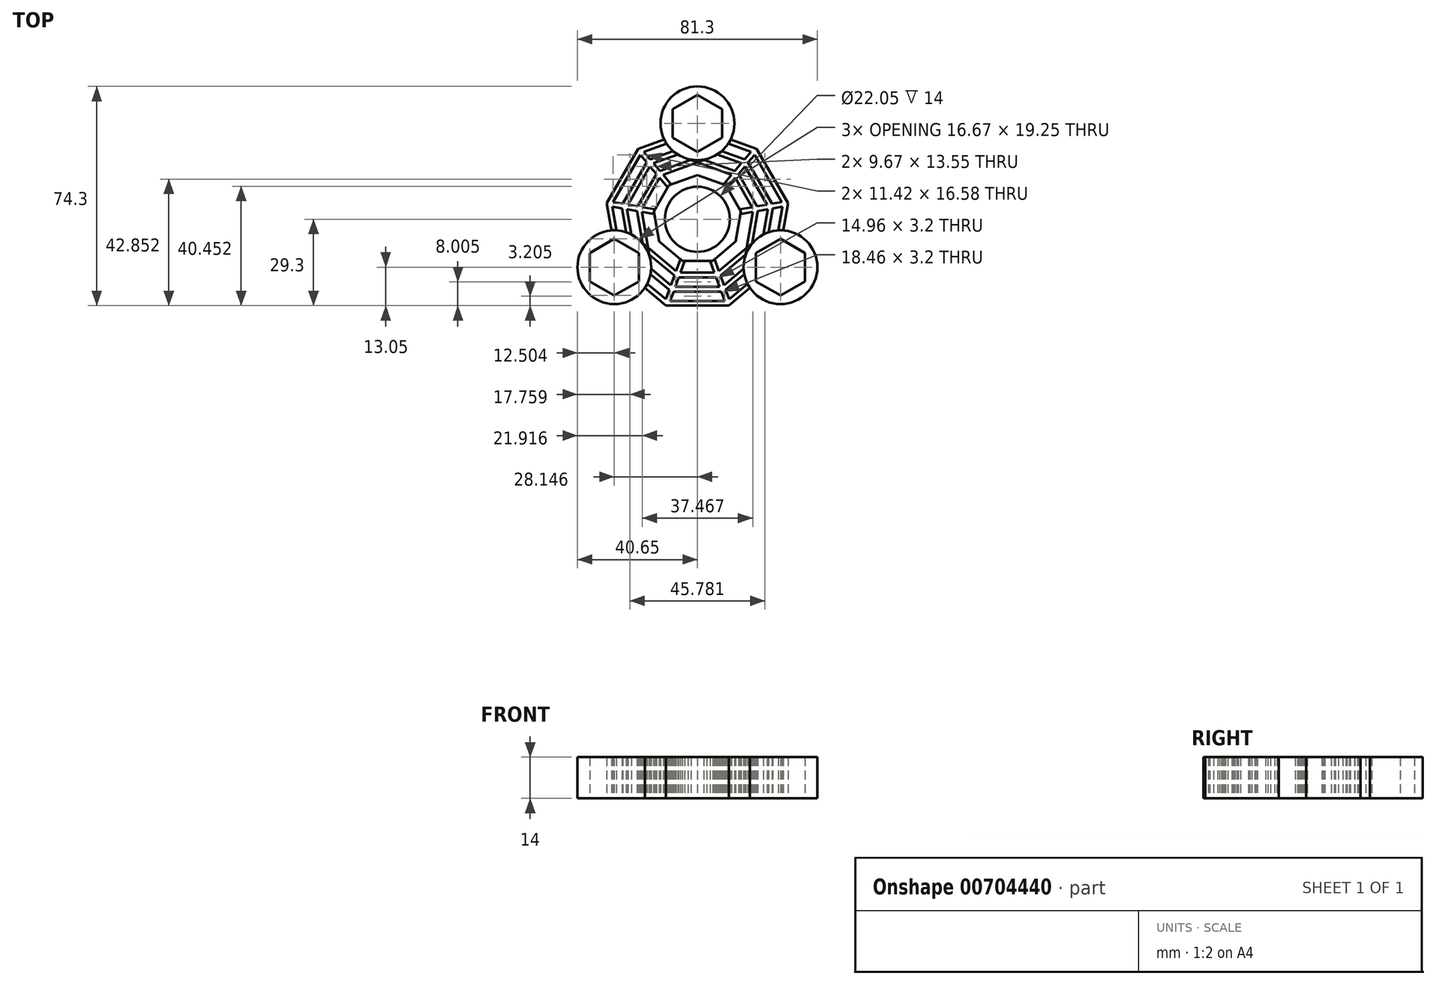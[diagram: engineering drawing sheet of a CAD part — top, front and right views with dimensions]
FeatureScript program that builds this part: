
annotation { "Feature Type Name" : "Feature", "Feature Type Description" : "" }
export const myFeature = defineFeature(function(context is Context, id is Id, definition is map)
    precondition{}
    {
        {
            var Q0;
            Q0=qCreatedBy(makeId("Top.planeOp"),FACE);
            var sketch = newSketch(context, id + "F0", { "sketchPlane" : qUnion([Q0])});
            skCircle(sketch, "E0", {"center": v(0, 0) * mm, "radius": 11.03 * mm});
            skCircle(sketch, "E1.cCircle", {"center": v(0, 32.5) * mm, "radius": 9.62 * mm, "construction": true});
            skLineSegment(sketch, "E1.0", {"start": v(8.34, 27.69) * mm, "end": v(0, 22.87) * mm});
            skLineSegment(sketch, "E1.1", {"start": v(0, 22.87) * mm, "end": v(-8.34, 27.69) * mm});
            skLineSegment(sketch, "E1.2", {"start": v(-8.34, 27.69) * mm, "end": v(-8.34, 37.31) * mm});
            skLineSegment(sketch, "E1.3", {"start": v(-8.34, 37.31) * mm, "end": v(0, 42.13) * mm});
            skLineSegment(sketch, "E1.4", {"start": v(0, 42.13) * mm, "end": v(8.34, 37.31) * mm});
            skLineSegment(sketch, "E1.5", {"start": v(8.34, 37.31) * mm, "end": v(8.34, 27.69) * mm});
            skCircle(sketch, "E2", {"center": v(0, 32.5) * mm, "radius": 12.5 * mm});
            skCircle(sketch, "E3.cCircle", {"center": v(0, 0) * mm, "radius": 15 * mm, "construction": true});
            skLineSegment(sketch, "E3.0", {"start": v(0, 15) * mm, "end": v(9.64, 11.5) * mm});
            skLineSegment(sketch, "E3.1", {"start": v(9.64, 11.5) * mm, "end": v(14.77, 2.6) * mm});
            skLineSegment(sketch, "E3.2", {"start": v(14.77, 2.6) * mm, "end": v(13, -7.5) * mm});
            skLineSegment(sketch, "E3.3", {"start": v(13, -7.5) * mm, "end": v(5.13, -14.1) * mm});
            skLineSegment(sketch, "E3.4", {"start": v(5.13, -14.1) * mm, "end": v(-5.13, -14.1) * mm});
            skLineSegment(sketch, "E3.5", {"start": v(-5.13, -14.1) * mm, "end": v(-13, -7.5) * mm});
            skLineSegment(sketch, "E3.6", {"start": v(-13, -7.5) * mm, "end": v(-14.77, 2.6) * mm});
            skLineSegment(sketch, "E3.7", {"start": v(-14.77, 2.6) * mm, "end": v(-9.64, 11.5) * mm});
            skLineSegment(sketch, "E3.8", {"start": v(-9.64, 11.5) * mm, "end": v(0, 15) * mm});
            skSolve(sketch);
        }
        {
            var Q0;
            Q0 = qSketchRegion(id + "F0", true);
            extrude(context, id + "F1", {"entities" : qUnion([Q0]), "depth" : 14 * mm, "offsetDistance" : 25 * mm});
        }
        {
            var Q0;
            Q0=makeQuery(id+"F1.opExtrude","SWEPT_BODY",BODY,{"disambiguationData":[OSD([sQuery(id+"F0.wireOp",EDGE,"E0"),sQuery(id+"F0.wireOp",EDGE,"V1B5BXI5-1Jbs-RwT4-ZZwz-bwv1kMuyMyS5"),sQuery(id+"F0.wireOp",EDGE,"E1.0"),sQuery(id+"F0.wireOp",EDGE,"E1.1"),sQuery(id+"F0.wireOp",EDGE,"E1.2"),sQuery(id+"F0.wireOp",EDGE,"E1.3"),sQuery(id+"F0.wireOp",EDGE,"E1.4"),sQuery(id+"F0.wireOp",EDGE,"E1.5"),sQuery(id+"F0.wireOp",EDGE,"E2"),sQuery(id+"F0.wireOp",EDGE,"70ad02f0-c52e-4f6c-8c91-bba6c70ca77e.0"),sQuery(id+"F0.wireOp",EDGE,"e65c8d9d-0cb7-4700-ba59-a3dc0d15118f.0"),sQuery(id+"F0.wireOp",EDGE,"d2b72db9-c3ad-4cec-af8e-b13c6486ea2f0.MirrorCS"),sQuery(id+"F0.wireOp",EDGE,"cb41e2ae-0834-4b17-9e15-60cb333e4af70.MirrorCS")])]});
            var Q1;
            Q1=makeQuery(id+"F1.opExtrude","SWEPT_FACE",FACE,{"disambiguationData":[OSD([sQuery(id+"F0.wireOp",EDGE,"E0")])]});
            circularPattern(context, id + "F2", {"entities" : qUnion([Q0]), "axis" : qUnion([Q1]), "angle" : 360 * degree, "instanceCount" : 3, "equalSpace" : true});
        }
        {
            var Q0;
            Q0=qCreatedBy(makeId("Top.planeOp"),FACE);
            var sketch = newSketch(context, id + "F3", { "sketchPlane" : qUnion([Q0])});
            skCircle(sketch, "E4.0", {"center": v(0, 32.5) * mm, "radius": 12.5 * mm});
            skCircle(sketch, "E5.0", {"center": v(28.15, -16.25) * mm, "radius": 12.5 * mm});
            skCircle(sketch, "E6.0", {"center": v(-28.15, -16.25) * mm, "radius": 12.5 * mm});
            skLineSegment(sketch, "E7", {"start": v(0, 0) * mm, "end": v(-32, 38.14) * mm, "construction": true});
            skLineSegment(sketch, "E8", {"start": v(0, 0) * mm, "end": v(-49.45, 8.72) * mm, "construction": true});
            skLineSegment(sketch, "E9", {"start": v(-29.08, -3.78) * mm, "end": v(-30.7, 5.41) * mm});
            skLineSegment(sketch, "E10", {"start": v(-30.7, 5.41) * mm, "end": v(-20.04, 23.88) * mm});
            skLineSegment(sketch, "E11", {"start": v(-20.04, 23.88) * mm, "end": v(-11.26, 27.08) * mm});
            skLineSegment(sketch, "E12", {"start": v(-27.46, -3.77) * mm, "end": v(-29.03, 5.12) * mm});
            skLineSegment(sketch, "E13", {"start": v(-29.03, 5.12) * mm, "end": v(-18.94, 22.58) * mm});
            skLineSegment(sketch, "E14", {"start": v(-18.94, 22.58) * mm, "end": v(-10.47, 25.66) * mm});
            skLineSegment(sketch, "E15", {"start": v(-24.1, -4.43) * mm, "end": v(-25.67, 4.53) * mm});
            skLineSegment(sketch, "E16", {"start": v(-25.67, 4.53) * mm, "end": v(-16.76, 19.97) * mm});
            skLineSegment(sketch, "E17", {"start": v(-16.76, 19.97) * mm, "end": v(-8.21, 23.08) * mm});
            skLineSegment(sketch, "E18", {"start": v(-22.33, -5.18) * mm, "end": v(-24, 4.23) * mm});
            skLineSegment(sketch, "E19", {"start": v(-24, 4.23) * mm, "end": v(-15.66, 18.66) * mm});
            skLineSegment(sketch, "E20", {"start": v(-15.66, 18.66) * mm, "end": v(-6.68, 21.93) * mm});
            skLineSegment(sketch, "E21", {"start": v(-18.55, -8.24) * mm, "end": v(-20.64, 3.64) * mm});
            skLineSegment(sketch, "E22", {"start": v(-20.64, 3.64) * mm, "end": v(-13.47, 16.06) * mm});
            skLineSegment(sketch, "E23", {"start": v(-13.47, 16.06) * mm, "end": v(-2.13, 20.18) * mm});
            skLineSegment(sketch, "E24", {"start": v(-16.1, -12.93) * mm, "end": v(-18.96, 3.34) * mm});
            skLineSegment(sketch, "E25", {"start": v(-18.96, 3.34) * mm, "end": v(-12.38, 14.75) * mm});
            skLineSegment(sketch, "E26", {"start": v(-12.38, 14.75) * mm, "end": v(3.15, 20.4) * mm});
            skLineSegment(sketch, "E27.0", {"start": v(-8.84, 11.78) * mm, "end": v(-31.39, 38.65) * mm});
            skLineSegment(sketch, "E28.0", {"start": v(-10.07, 10.75) * mm, "end": v(-32.61, 37.62) * mm});
            skLineSegment(sketch, "E29.0", {"start": v(-14.35, 3.34) * mm, "end": v(-49.31, 9.5) * mm});
            skLineSegment(sketch, "E30.0", {"start": v(-14.62, 1.77) * mm, "end": v(-49.6, 7.93) * mm});
            skLineSegment(sketch, "E31.0", {"start": v(-13, -7.5) * mm, "end": v(-14.77, 2.6) * mm});
            skLineSegment(sketch, "E32.0.0", {"start": v(0, 15) * mm, "end": v(-9.64, 11.5) * mm});
            skLineSegment(sketch, "E32.0.1", {"start": v(-9.64, 11.5) * mm, "end": v(-14.77, 2.6) * mm});
            skLineSegment(sketch, "E32.0.2", {"start": v(-14.77, 2.6) * mm, "end": v(-13, -7.5) * mm});
            skLineSegment(sketch, "E32.0.3", {"start": v(-13, -7.5) * mm, "end": v(-5.13, -14.1) * mm});
            skLineSegment(sketch, "E32.0.4", {"start": v(-5.13, -14.1) * mm, "end": v(5.13, -14.1) * mm});
            skLineSegment(sketch, "E32.0.5", {"start": v(5.13, -14.1) * mm, "end": v(13, -7.5) * mm});
            skLineSegment(sketch, "E32.0.6", {"start": v(13, -7.5) * mm, "end": v(14.77, 2.6) * mm});
            skLineSegment(sketch, "E32.0.7", {"start": v(14.77, 2.6) * mm, "end": v(9.64, 11.5) * mm});
            skLineSegment(sketch, "E32.0.8", {"start": v(9.64, 11.5) * mm, "end": v(0, 15) * mm});
            skSolve(sketch);
        }
        {
            var Q0;
            {var subQ3=sQuery(id+"F3.wireOp",EDGE,"E25");var subQ5=sQuery(id+"F3.wireOp",EDGE,"E24");var subQ6=makeQuery(id+"F3.imprint","INTERSECT",VERTEX,{"derivedFrom":[subQ5,subQ3]});Q0=makeQuery(id+"F3.imprint","IMPRINT",FACE,{"disambiguationData":[TD([[makeQuery(id+"F3.imprint","IMPRINT",EDGE,{"disambiguationData":[TD([[subQ6,1.0]])],"derivedFrom":subQ5}),-1.0]])]});}
            var Q1;
            {var subQ3=sQuery(id+"F3.wireOp",EDGE,"E26");var subQ7=sQuery(id+"F3.wireOp",EDGE,"E25");var subQ8=makeQuery(id+"F3.imprint","INTERSECT",VERTEX,{"derivedFrom":[subQ7,subQ3]});Q1=makeQuery(id+"F3.imprint","IMPRINT",FACE,{"disambiguationData":[TD([[makeQuery(id+"F3.imprint","IMPRINT",EDGE,{"disambiguationData":[TD([[subQ8,1.0]])],"derivedFrom":subQ7}),-1.0]])]});}
            var Q2;
            {var subQ5=sQuery(id+"F3.wireOp",EDGE,"E22");var subQ9=sQuery(id+"F3.wireOp",EDGE,"E21");var subQ10=makeQuery(id+"F3.imprint","INTERSECT",VERTEX,{"derivedFrom":[subQ9,subQ5]});Q2=makeQuery(id+"F3.imprint","IMPRINT",FACE,{"disambiguationData":[TD([[makeQuery(id+"F3.imprint","IMPRINT",EDGE,{"disambiguationData":[TD([[subQ10,1.0]])],"derivedFrom":subQ9}),-1.0]])]});}
            var Q3;
            {var subQ7=sQuery(id+"F3.wireOp",EDGE,"E23");var subQ8=sQuery(id+"F3.wireOp",EDGE,"E22");var subQ9=makeQuery(id+"F3.imprint","INTERSECT",VERTEX,{"derivedFrom":[subQ8,subQ7]});Q3=makeQuery(id+"F3.imprint","IMPRINT",FACE,{"disambiguationData":[TD([[makeQuery(id+"F3.imprint","IMPRINT",EDGE,{"disambiguationData":[TD([[subQ9,1.0]])],"derivedFrom":subQ8}),-1.0]])]});}
            var Q4;
            {var subQ7=sQuery(id+"F3.wireOp",EDGE,"E19");var subQ9=sQuery(id+"F3.wireOp",EDGE,"E20");var subQ10=makeQuery(id+"F3.imprint","INTERSECT",VERTEX,{"derivedFrom":[subQ7,subQ9]});Q4=makeQuery(id+"F3.imprint","IMPRINT",FACE,{"disambiguationData":[TD([[makeQuery(id+"F3.imprint","IMPRINT",EDGE,{"disambiguationData":[TD([[subQ10,1.0]])],"derivedFrom":subQ7}),-1.0]])]});}
            var Q5;
            {var subQ7=sQuery(id+"F3.wireOp",EDGE,"E19");var subQ8=sQuery(id+"F3.wireOp",EDGE,"E18");var subQ9=makeQuery(id+"F3.imprint","INTERSECT",VERTEX,{"derivedFrom":[subQ8,subQ7]});Q5=makeQuery(id+"F3.imprint","IMPRINT",FACE,{"disambiguationData":[TD([[makeQuery(id+"F3.imprint","IMPRINT",EDGE,{"disambiguationData":[TD([[subQ9,1.0]])],"derivedFrom":subQ8}),-1.0]])]});}
            var Q6;
            {var subQ6=sQuery(id+"F3.wireOp",EDGE,"E15");var subQ9=sQuery(id+"F3.wireOp",EDGE,"E16");var subQ10=makeQuery(id+"F3.imprint","INTERSECT",VERTEX,{"derivedFrom":[subQ6,subQ9]});Q6=makeQuery(id+"F3.imprint","IMPRINT",FACE,{"disambiguationData":[TD([[makeQuery(id+"F3.imprint","IMPRINT",EDGE,{"disambiguationData":[TD([[subQ10,1.0]])],"derivedFrom":subQ6}),-1.0]])]});}
            var Q7;
            {var subQ7=sQuery(id+"F3.wireOp",EDGE,"E17");var subQ8=sQuery(id+"F3.wireOp",EDGE,"E16");var subQ9=makeQuery(id+"F3.imprint","INTERSECT",VERTEX,{"derivedFrom":[subQ8,subQ7]});Q7=makeQuery(id+"F3.imprint","IMPRINT",FACE,{"disambiguationData":[TD([[makeQuery(id+"F3.imprint","IMPRINT",EDGE,{"disambiguationData":[TD([[subQ9,1.0]])],"derivedFrom":subQ8}),-1.0]])]});}
            var Q8;
            {var subQ7=sQuery(id+"F3.wireOp",EDGE,"E14");var subQ8=sQuery(id+"F3.wireOp",EDGE,"E13");var subQ9=makeQuery(id+"F3.imprint","INTERSECT",VERTEX,{"derivedFrom":[subQ8,subQ7]});Q8=makeQuery(id+"F3.imprint","IMPRINT",FACE,{"disambiguationData":[TD([[makeQuery(id+"F3.imprint","IMPRINT",EDGE,{"disambiguationData":[TD([[subQ9,1.0]])],"derivedFrom":subQ8}),-1.0]])]});}
            var Q9;
            {var subQ7=sQuery(id+"F3.wireOp",EDGE,"E13");var subQ8=sQuery(id+"F3.wireOp",EDGE,"E12");var subQ9=makeQuery(id+"F3.imprint","INTERSECT",VERTEX,{"derivedFrom":[subQ8,subQ7]});Q9=makeQuery(id+"F3.imprint","IMPRINT",FACE,{"disambiguationData":[TD([[makeQuery(id+"F3.imprint","IMPRINT",EDGE,{"disambiguationData":[TD([[subQ9,1.0]])],"derivedFrom":subQ8}),-1.0]])]});}
            var Q10;
            {var subQ7=sQuery(id+"F3.wireOp",EDGE,"E10");var subQ9=sQuery(id+"F3.wireOp",EDGE,"E9");var subQ10=makeQuery(id+"F3.imprint","INTERSECT",VERTEX,{"derivedFrom":[subQ9,subQ7]});Q10=makeQuery(id+"F3.imprint","IMPRINT",FACE,{"disambiguationData":[TD([[makeQuery(id+"F3.imprint","IMPRINT",EDGE,{"disambiguationData":[TD([[subQ10,1.0]])],"derivedFrom":subQ9}),-1.0]])]});}
            var Q11;
            {var subQ7=sQuery(id+"F3.wireOp",EDGE,"E11");var subQ8=sQuery(id+"F3.wireOp",EDGE,"E10");var subQ9=makeQuery(id+"F3.imprint","INTERSECT",VERTEX,{"derivedFrom":[subQ8,subQ7]});Q11=makeQuery(id+"F3.imprint","IMPRINT",FACE,{"disambiguationData":[TD([[makeQuery(id+"F3.imprint","IMPRINT",EDGE,{"disambiguationData":[TD([[subQ9,1.0]])],"derivedFrom":subQ8}),-1.0]])]});}
            var Q12;
            {var subQ0=sQuery(id+"F3.wireOp",EDGE,"E11");var subQ1=sQuery(id+"F3.wireOp",EDGE,"E4.0");var subQ2=makeQuery(id+"F3.imprint","INTERSECT",VERTEX,{"derivedFrom":[subQ1,subQ0]});Q12=makeQuery(id+"F3.imprint","IMPRINT",FACE,{"disambiguationData":[TD([[makeQuery(id+"F3.imprint","IMPRINT",EDGE,{"disambiguationData":[TD([[subQ2,-1.0]])],"derivedFrom":subQ1}),-1.0]])]});}
            var Q13;
            {var subQ0=sQuery(id+"F3.wireOp",EDGE,"E29.0");var subQ1=sQuery(id+"F3.wireOp",EDGE,"E10");var subQ2=makeQuery(id+"F3.imprint","INTERSECT",VERTEX,{"derivedFrom":[subQ1,subQ0]});Q13=makeQuery(id+"F3.imprint","IMPRINT",FACE,{"disambiguationData":[TD([[makeQuery(id+"F3.imprint","IMPRINT",EDGE,{"disambiguationData":[TD([[subQ2,-1.0]])],"derivedFrom":subQ1}),-1.0]])]});}
            var Q14;
            {var subQ0=sQuery(id+"F3.wireOp",EDGE,"E9");var subQ1=sQuery(id+"F3.wireOp",EDGE,"E5.0");var subQ2=makeQuery(id+"F3.imprint","INTERSECT",VERTEX,{"derivedFrom":[subQ1,subQ0]});Q14=makeQuery(id+"F3.imprint","IMPRINT",FACE,{"disambiguationData":[TD([[makeQuery(id+"F3.imprint","IMPRINT",EDGE,{"disambiguationData":[TD([[subQ2,1.0]])],"derivedFrom":subQ1}),-1.0]])]});}
            var Q15;
            {var subQ0=sQuery(id+"F3.wireOp",EDGE,"E15");var subQ1=sQuery(id+"F3.wireOp",EDGE,"E5.0");var subQ2=makeQuery(id+"F3.imprint","INTERSECT",VERTEX,{"derivedFrom":[subQ1,subQ0]});Q15=makeQuery(id+"F3.imprint","IMPRINT",FACE,{"disambiguationData":[TD([[makeQuery(id+"F3.imprint","IMPRINT",EDGE,{"disambiguationData":[TD([[subQ2,1.0]])],"derivedFrom":subQ1}),-1.0]])]});}
            var Q16;
            {var subQ0=sQuery(id+"F3.wireOp",EDGE,"E29.0");var subQ1=sQuery(id+"F3.wireOp",EDGE,"E16");var subQ2=makeQuery(id+"F3.imprint","INTERSECT",VERTEX,{"derivedFrom":[subQ1,subQ0]});Q16=makeQuery(id+"F3.imprint","IMPRINT",FACE,{"disambiguationData":[TD([[makeQuery(id+"F3.imprint","IMPRINT",EDGE,{"disambiguationData":[TD([[subQ2,-1.0]])],"derivedFrom":subQ1}),-1.0]])]});}
            var Q17;
            {var subQ0=sQuery(id+"F3.wireOp",EDGE,"E17");var subQ1=sQuery(id+"F3.wireOp",EDGE,"E4.0");var subQ2=makeQuery(id+"F3.imprint","INTERSECT",VERTEX,{"derivedFrom":[subQ1,subQ0]});Q17=makeQuery(id+"F3.imprint","IMPRINT",FACE,{"disambiguationData":[TD([[makeQuery(id+"F3.imprint","IMPRINT",EDGE,{"disambiguationData":[TD([[subQ2,-1.0]])],"derivedFrom":subQ1}),-1.0]])]});}
            var Q18;
            {var subQ0=sQuery(id+"F3.wireOp",EDGE,"E23");var subQ1=sQuery(id+"F3.wireOp",EDGE,"E4.0");var subQ2=makeQuery(id+"F3.imprint","INTERSECT",VERTEX,{"derivedFrom":[subQ1,subQ0]});Q18=makeQuery(id+"F3.imprint","IMPRINT",FACE,{"disambiguationData":[TD([[makeQuery(id+"F3.imprint","IMPRINT",EDGE,{"disambiguationData":[TD([[subQ2,-1.0]])],"derivedFrom":subQ1}),-1.0]])]});}
            var Q19;
            {var subQ0=sQuery(id+"F3.wireOp",EDGE,"E29.0");var subQ1=sQuery(id+"F3.wireOp",EDGE,"E22");var subQ2=makeQuery(id+"F3.imprint","INTERSECT",VERTEX,{"derivedFrom":[subQ1,subQ0]});Q19=makeQuery(id+"F3.imprint","IMPRINT",FACE,{"disambiguationData":[TD([[makeQuery(id+"F3.imprint","IMPRINT",EDGE,{"disambiguationData":[TD([[subQ2,-1.0]])],"derivedFrom":subQ1}),-1.0]])]});}
            var Q20;
            {var subQ0=sQuery(id+"F3.wireOp",EDGE,"E21");var subQ1=sQuery(id+"F3.wireOp",EDGE,"E5.0");var subQ2=makeQuery(id+"F3.imprint","INTERSECT",VERTEX,{"derivedFrom":[subQ1,subQ0]});Q20=makeQuery(id+"F3.imprint","IMPRINT",FACE,{"disambiguationData":[TD([[makeQuery(id+"F3.imprint","IMPRINT",EDGE,{"disambiguationData":[TD([[subQ2,1.0]])],"derivedFrom":subQ1}),-1.0]])]});}
            var Q21;
            {var subQ0=sQuery(id+"F3.wireOp",EDGE,"E6.0");var subQ1=sQuery(id+"F3.wireOp",EDGE,"E9");var subQ2=makeQuery(id+"F3.imprint","INTERSECT",VERTEX,{"derivedFrom":[subQ1,subQ0]});Q21=makeQuery(id+"F3.imprint","IMPRINT",FACE,{"disambiguationData":[TD([[makeQuery(id+"F3.imprint","IMPRINT",EDGE,{"disambiguationData":[TD([[subQ2,-1.0]])],"derivedFrom":subQ1}),-1.0]])]});}
            var Q22;
            {var subQ0=sQuery(id+"F3.wireOp",EDGE,"E6.0");var subQ1=sQuery(id+"F3.wireOp",EDGE,"E15");var subQ2=makeQuery(id+"F3.imprint","INTERSECT",VERTEX,{"derivedFrom":[subQ1,subQ0]});Q22=makeQuery(id+"F3.imprint","IMPRINT",FACE,{"disambiguationData":[TD([[makeQuery(id+"F3.imprint","IMPRINT",EDGE,{"disambiguationData":[TD([[subQ2,-1.0]])],"derivedFrom":subQ1}),-1.0]])]});}
            var Q23;
            {var subQ0=sQuery(id+"F3.wireOp",EDGE,"E6.0");var subQ1=sQuery(id+"F3.wireOp",EDGE,"E21");var subQ2=makeQuery(id+"F3.imprint","INTERSECT",VERTEX,{"derivedFrom":[subQ1,subQ0]});Q23=makeQuery(id+"F3.imprint","IMPRINT",FACE,{"disambiguationData":[TD([[makeQuery(id+"F3.imprint","IMPRINT",EDGE,{"disambiguationData":[TD([[subQ2,-1.0]])],"derivedFrom":subQ1}),-1.0]])]});}
            var Q24;
            Q24=makeQuery(id+"F1.opExtrude","CAP_FACE",FACE,{"disambiguationData":[OSD([sQuery(id+"F0.wireOp",EDGE,"E1.0"),sQuery(id+"F0.wireOp",EDGE,"E1.1"),sQuery(id+"F0.wireOp",EDGE,"E1.2"),sQuery(id+"F0.wireOp",EDGE,"E1.3"),sQuery(id+"F0.wireOp",EDGE,"E1.4"),sQuery(id+"F0.wireOp",EDGE,"E1.5"),sQuery(id+"F0.wireOp",EDGE,"E2")])],"isStart":false});
            extrude(context, id + "F4", {"entities" : qUnion([Q0, Q1, Q2, Q3, Q4, Q5, Q6, Q7, Q8, Q9, Q10, Q11, Q12, Q13, Q14, Q15, Q16, Q17, Q18, Q19, Q20, Q21, Q22, Q23]), "endBound" : BoundingType.UP_TO_SURFACE, "depth" : 14 * mm, "endBoundEntityFace" : qUnion([Q24]), "offsetDistance" : 25 * mm});
        }
        {
            var Q0;
            Q0=makeQuery(id+"F4.opExtrude","SWEPT_BODY",BODY,{"disambiguationData":[OSD([sQuery(id+"F3.wireOp",EDGE,"E4.0"),sQuery(id+"F3.wireOp",EDGE,"E5.0"),sQuery(id+"F3.wireOp",EDGE,"E9"),sQuery(id+"F3.wireOp",EDGE,"E10"),sQuery(id+"F3.wireOp",EDGE,"E11"),sQuery(id+"F3.wireOp",EDGE,"E12"),sQuery(id+"F3.wireOp",EDGE,"E13"),sQuery(id+"F3.wireOp",EDGE,"E14"),sQuery(id+"F3.wireOp",EDGE,"E15"),sQuery(id+"F3.wireOp",EDGE,"E16"),sQuery(id+"F3.wireOp",EDGE,"E17"),sQuery(id+"F3.wireOp",EDGE,"E18"),sQuery(id+"F3.wireOp",EDGE,"E19"),sQuery(id+"F3.wireOp",EDGE,"E20"),sQuery(id+"F3.wireOp",EDGE,"E21"),sQuery(id+"F3.wireOp",EDGE,"E22"),sQuery(id+"F3.wireOp",EDGE,"E23"),sQuery(id+"F3.wireOp",EDGE,"E24"),sQuery(id+"F3.wireOp",EDGE,"E25"),sQuery(id+"F3.wireOp",EDGE,"E26"),sQuery(id+"F3.wireOp",EDGE,"5fbdd46c-726b-4fb3-8af4-6456a0da1a19.0"),sQuery(id+"F3.wireOp",EDGE,"E27.0"),sQuery(id+"F3.wireOp",EDGE,"E28.0"),sQuery(id+"F3.wireOp",EDGE,"E29.0"),sQuery(id+"F3.wireOp",EDGE,"E30.0")])]});
            var Q1;
            Q1=makeQuery(id+"F1.opExtrude","SWEPT_FACE",FACE,{"disambiguationData":[OSD([sQuery(id+"F0.wireOp",EDGE,"E0")])]});
            circularPattern(context, id + "F5", {"entities" : qUnion([Q0]), "axis" : qUnion([Q1]), "angle" : 360 * degree, "instanceCount" : 3, "equalSpace" : true});
        }
    });
